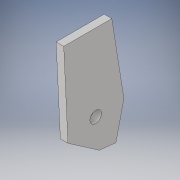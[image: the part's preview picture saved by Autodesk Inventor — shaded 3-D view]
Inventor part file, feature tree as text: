
AUTODESK INVENTOR PART (.ipt)
format: ipt  version: 2018 (Build 220112000, 112)  size: 100,352 bytes
history: native  units: in
note: dims shown in document units (in); Inventor stores cm internally (conversion verified against a paired STEP export)
features: extrude x1, sketch x1
ambient origin geometry x8: Origin, YZ Plane, XZ Plane, XY Plane, X Axis, Y Axis, Z Axis, Center Point
bodies: Solid1 (feature_tree)
feature tree (2):
  extrude  "Extrusion1"  Depth=0.2in
  sketch  "Sketch1"  dims[d0=1.26in d1=1.0in d2=0.3in d3=2.02in d4=0.2in d5=0.0in]
